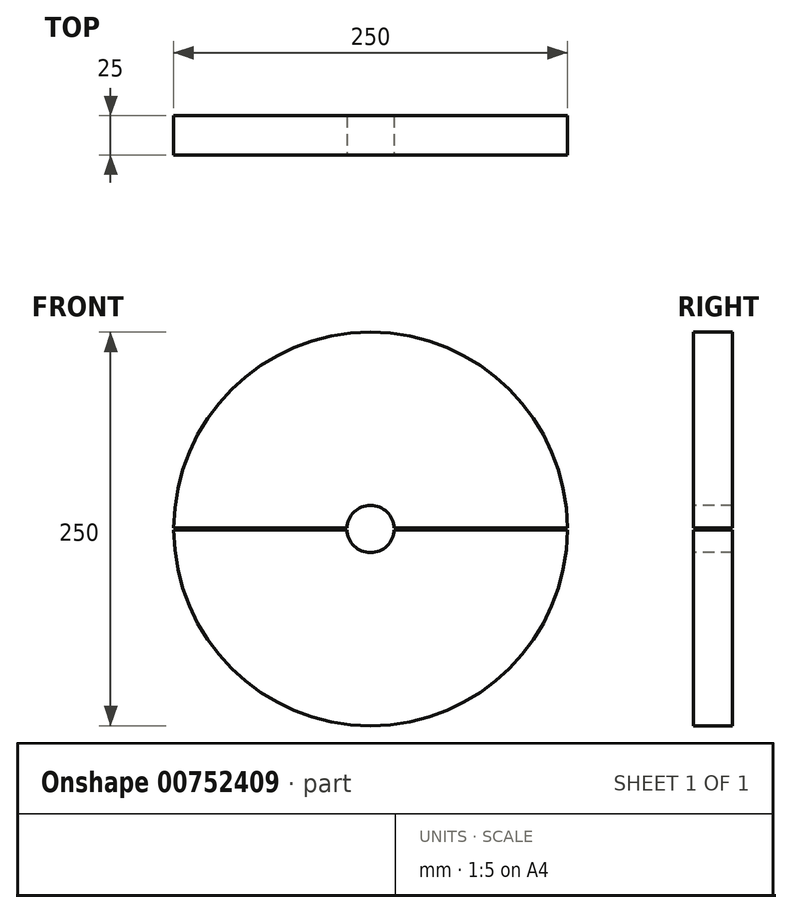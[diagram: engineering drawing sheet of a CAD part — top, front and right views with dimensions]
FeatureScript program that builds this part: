
annotation { "Feature Type Name" : "Feature", "Feature Type Description" : "" }
export const myFeature = defineFeature(function(context is Context, id is Id, definition is map)
    precondition{}
    {
        {
            var Q0;
            Q0=qCreatedBy(makeId("Front.planeOp"),FACE);
            var sketch = newSketch(context, id + "F0", { "sketchPlane" : qUnion([Q0])});
            skCircle(sketch, "E0", {"center": v(0, 0) * mm, "radius": 125 * mm});
            skSolve(sketch);
        }
        {
            var Q0;
            Q0 = qSketchRegion(id + "F0", true);
            extrude(context, id + "F1", {"entities" : qUnion([Q0]), "depth" : 25 * mm, "offsetDistance" : 25 * mm});
        }
        {
            var Q0;
            Q0=makeQuery(id+"F1.opExtrude","CAP_FACE",FACE,{"disambiguationData":[OSD([sQuery(id+"F0.wireOp",EDGE,"E0")])],"isStart":false});
            var sketch = newSketch(context, id + "F2", { "sketchPlane" : qUnion([Q0])});
            skCircle(sketch, "E1", {"center": v(0, 0) * mm, "radius": 15 * mm});
            skSolve(sketch);
        }
        {
            var Q0;
            Q0 = qSketchRegion(id + "F2", true);
            extrude(context, id + "F3", {"entities" : qUnion([Q0]), "operationType" : NewBodyOperationType.REMOVE, "oppositeDirection" : true, "depth" : 25 * mm, "offsetDistance" : 25 * mm});
        }
        {
            var Q0;
            Q0=makeQuery(id+"F1.opExtrude","CAP_FACE",FACE,{"disambiguationData":[OSD([sQuery(id+"F0.wireOp",EDGE,"E0")])],"isStart":false});
            var sketch = newSketch(context, id + "F4", { "sketchPlane" : qUnion([Q0])});
            skLineSegment(sketch, "E2.bottom", {"start": v(-268.1, -0.5) * mm, "end": v(231.9, -0.5) * mm});
            skLineSegment(sketch, "E2.top", {"start": v(-268.1, 0.5) * mm, "end": v(231.9, 0.5) * mm});
            skLineSegment(sketch, "E2.left", {"start": v(-268.1, -0.5) * mm, "end": v(-268.1, 0.5) * mm});
            skLineSegment(sketch, "E2.right", {"start": v(231.9, -0.5) * mm, "end": v(231.9, 0.5) * mm});
            skSolve(sketch);
        }
        {
            var Q0;
            Q0 = qSketchRegion(id + "F4", true);
            extrude(context, id + "F5", {"entities" : qUnion([Q0]), "operationType" : NewBodyOperationType.REMOVE, "oppositeDirection" : true, "depth" : 25 * mm, "offsetDistance" : 25 * mm});
        }
    });
